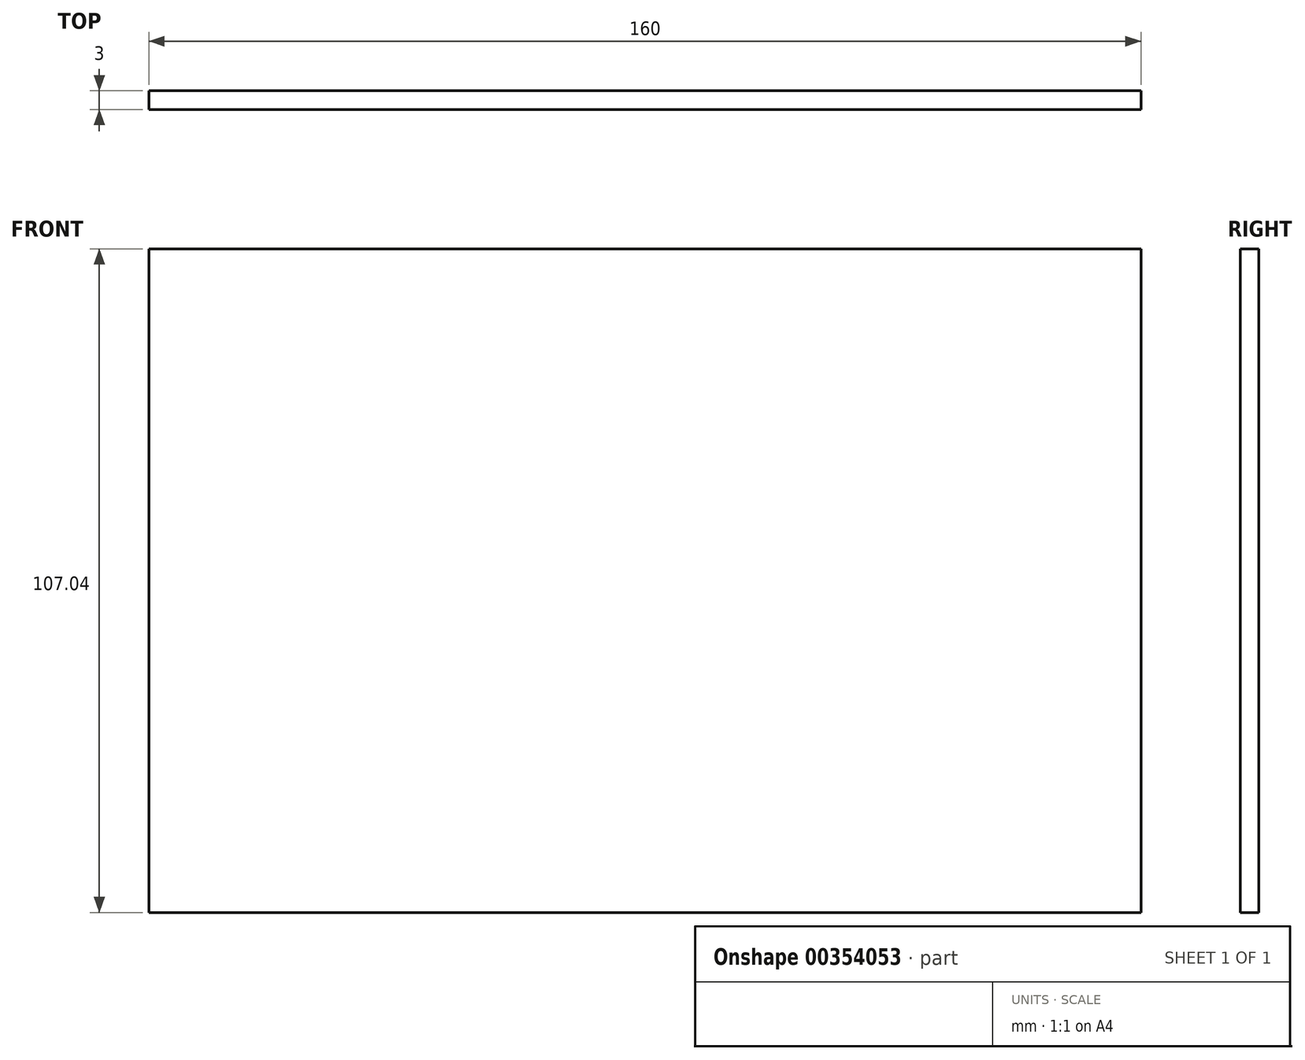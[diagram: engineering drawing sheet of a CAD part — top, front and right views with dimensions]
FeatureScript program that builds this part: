
annotation { "Feature Type Name" : "Feature", "Feature Type Description" : "" }
export const myFeature = defineFeature(function(context is Context, id is Id, definition is map)
    precondition{}
    {
        {
            var Q0;
            Q0=qCreatedBy(makeId("Front.planeOp"),FACE);
            var sketch = newSketch(context, id + "F0", { "sketchPlane" : qUnion([Q0])});
            skLineSegment(sketch, "E0.bottom", {"start": v(-91.31, 50.56) * mm, "end": v(68.69, 50.56) * mm});
            skLineSegment(sketch, "E0.top", {"start": v(-91.31, -56.48) * mm, "end": v(68.69, -56.48) * mm});
            skLineSegment(sketch, "E0.left", {"start": v(-91.31, 50.56) * mm, "end": v(-91.31, -56.48) * mm});
            skLineSegment(sketch, "E0.right", {"start": v(68.69, 50.56) * mm, "end": v(68.69, -56.48) * mm});
            skSolve(sketch);
        }
        {
            var Q0;
            Q0 = qSketchRegion(id + "F0", true);
            extrude(context, id + "F1", {"entities" : qUnion([Q0]), "depth" : 3 * mm});
        }
    });
